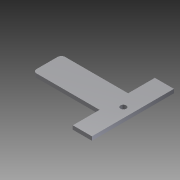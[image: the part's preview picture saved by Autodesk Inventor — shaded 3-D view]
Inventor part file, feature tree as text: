
AUTODESK INVENTOR PART (.ipt)
format: ipt  version: 2012 (Build 160160000, 160)  size: 84,480 bytes
history: native  units: mm
features: extrude x1, sketch x1
ambient origin geometry x8: Origin, YZ Plane, XZ Plane, XY Plane, X Axis, Y Axis, Z Axis, Center Point
bodies: Solid1 (feature_tree)
feature tree (2):
  extrude  "Extrusion1"  Depth=2.0mm TaperAngle=0.0deg
  sketch  "Sketch1"  dims[d0=35.0mm d1=2.0mm d2=10.0mm d3=43.0mm d4=10.0mm d5=14.0mm d6=14.0mm d7=3.0mm d8=5.0mm d9=21.5mm d10=2.0mm d11=0.0mm]
